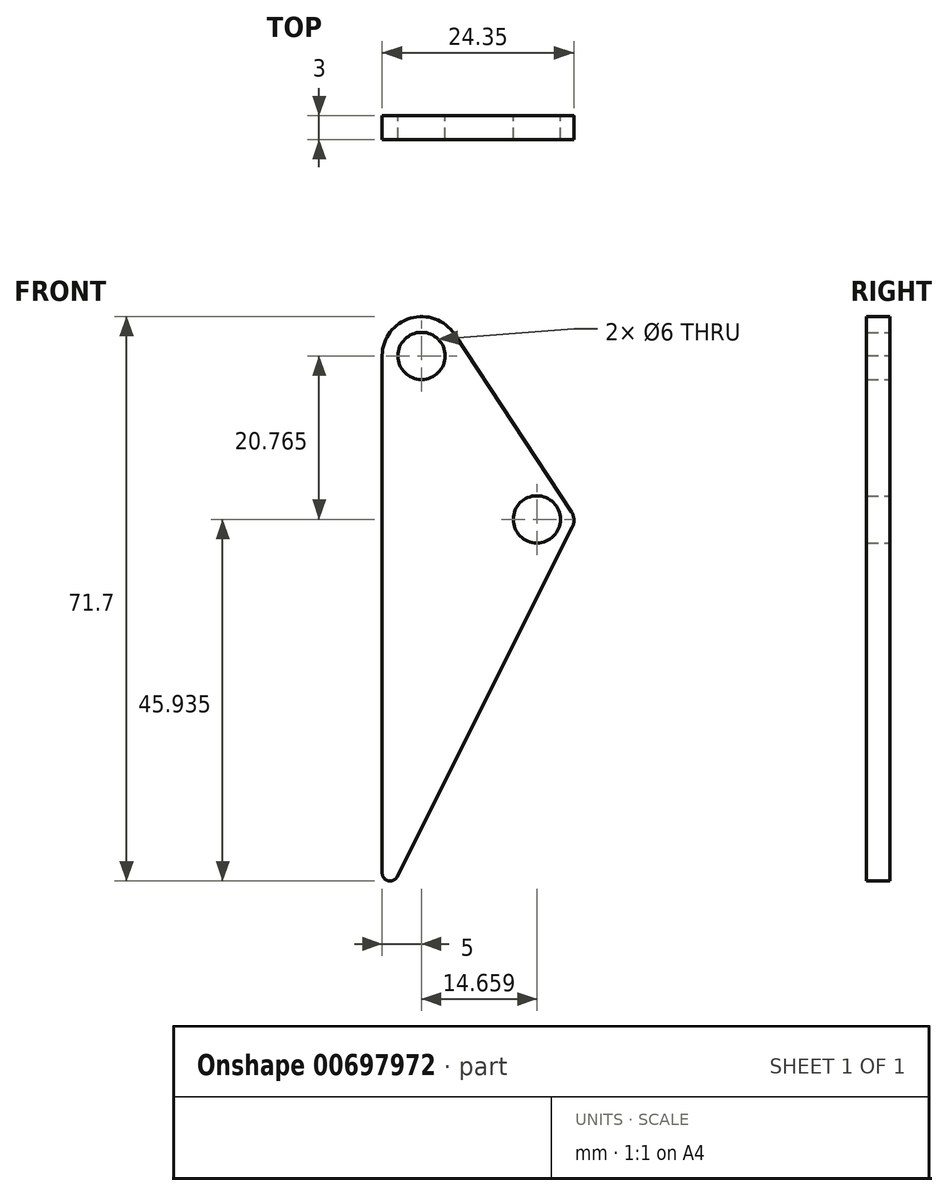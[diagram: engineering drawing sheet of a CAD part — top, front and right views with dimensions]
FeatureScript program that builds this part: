
annotation { "Feature Type Name" : "Feature", "Feature Type Description" : "" }
export const myFeature = defineFeature(function(context is Context, id is Id, definition is map)
    precondition{}
    {
        {
            var Q0;
            Q0=qCreatedBy(makeId("Front.planeOp"),FACE);
            var sketch = newSketch(context, id + "F0", { "sketchPlane" : qUnion([Q0])});
            skCircle(sketch, "E0", {"center": v(0, 0) * mm, "radius": 3 * mm});
            skArc(sketch, "E1", {"start": v(4.18, 2.75) * mm, "mid": v(-1.4, 4.8) * mm, "end": v(-5, 0.07) * mm});
            skLineSegment(sketch, "E2", {"start": v(-5, 0.07) * mm, "end": v(-5, -65.7) * mm});
            skLineSegment(sketch, "E3", {"start": v(-3.1, -66.15) * mm, "end": v(19.14, -21.8) * mm});
            skLineSegment(sketch, "E4", {"start": v(19.02, -19.8) * mm, "end": v(4.18, 2.75) * mm});
            skPoint(sketch, "E5.visualSharp", {"position": v(-5, -69.93) * mm});
            skArc(sketch, "E5.filletArc", {"start": v(-5, -65.7) * mm, "mid": v(-4.23, -66.68) * mm, "end": v(-3.1, -66.15) * mm});
            skPoint(sketch, "E6.visualSharp", {"position": v(19.66, -20.77) * mm});
            skArc(sketch, "E6.filletArc", {"start": v(19.14, -21.8) * mm, "mid": v(19.35, -20.78) * mm, "end": v(19.02, -19.8) * mm});
            skCircle(sketch, "E7", {"center": v(14.66, -20.77) * mm, "radius": 3 * mm});
            skSolve(sketch);
        }
        {
            var Q0;
            Q0=makeQuery(id+"F0.imprint","IMPRINT",FACE,{"disambiguationData":[TD([[makeQuery(id+"F0.imprint","IMPRINT",EDGE,{"derivedFrom":sQuery(id+"F0.wireOp",EDGE,"E0")}),-1.0]])]});
            extrude(context, id + "F1", {"entities" : qUnion([Q0]), "depth" : 3 * mm, "offsetDistance" : 25 * mm});
        }
    });
